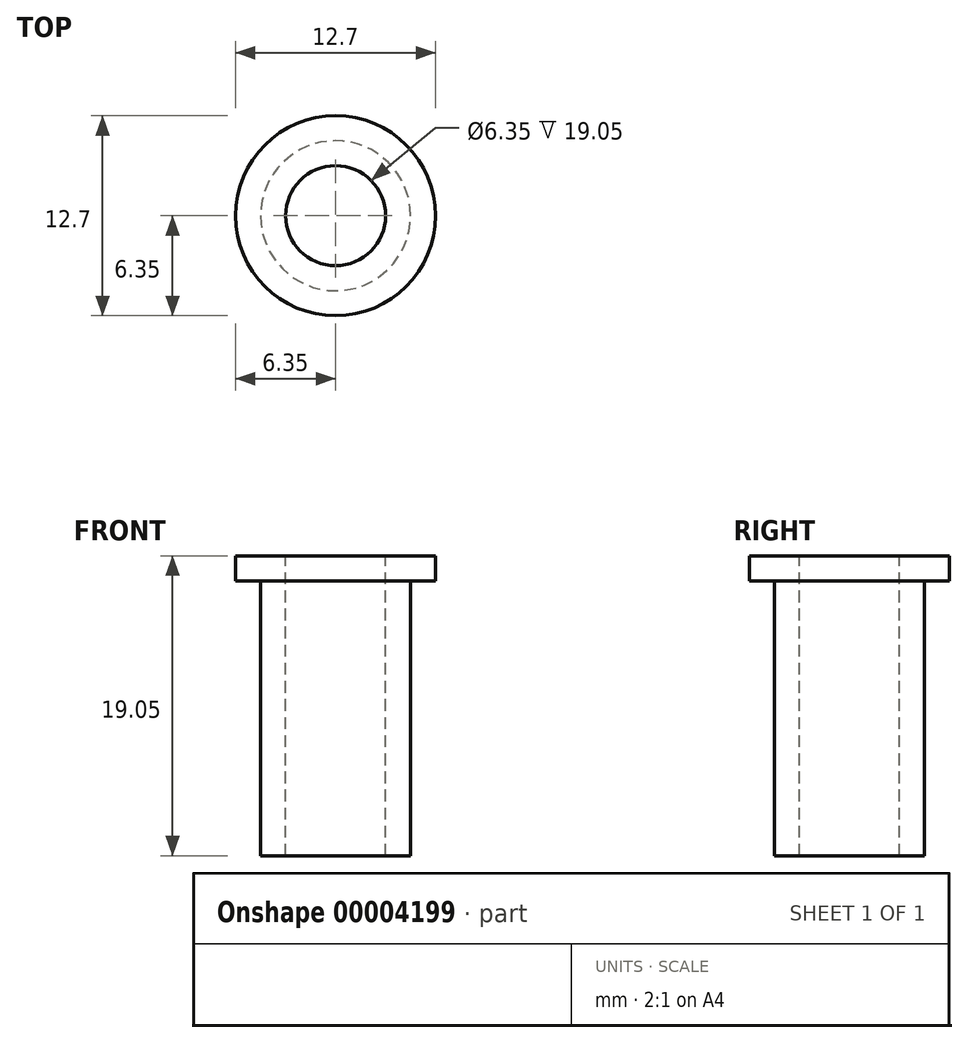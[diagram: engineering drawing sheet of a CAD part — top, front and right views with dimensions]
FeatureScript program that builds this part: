
annotation { "Feature Type Name" : "Feature", "Feature Type Description" : "" }
export const myFeature = defineFeature(function(context is Context, id is Id, definition is map)
    precondition{}
    {
        {
            var Q0;
            Q0=qCreatedBy(makeId("Front.planeOp"),FACE);
            var sketch = newSketch(context, id + "F0", { "sketchPlane" : qUnion([Q0])});
            skLineSegment(sketch, "E0", {"start": v(6.35, 0) * mm, "end": v(3.18, 0) * mm});
            skLineSegment(sketch, "E1", {"start": v(3.18, 0) * mm, "end": v(3.18, -19.05) * mm});
            skLineSegment(sketch, "E2", {"start": v(3.18, -19.05) * mm, "end": v(4.76, -19.05) * mm});
            skLineSegment(sketch, "E3", {"start": v(4.76, -19.05) * mm, "end": v(4.76, -1.59) * mm});
            skLineSegment(sketch, "E4", {"start": v(4.76, -1.59) * mm, "end": v(6.35, -1.59) * mm});
            skLineSegment(sketch, "E5", {"start": v(6.35, -1.59) * mm, "end": v(6.35, 0) * mm});
            skLineSegment(sketch, "E6", {"start": v(0, 0) * mm, "end": v(0, -18.07) * mm, "construction": true});
            skSolve(sketch);
        }
        {
            var Q0;
            Q0=makeQuery(id+"F0.imprint","IMPRINT",FACE,{"disambiguationData":[TD([[makeQuery(id+"F0.imprint","IMPRINT",EDGE,{"derivedFrom":sQuery(id+"F0.wireOp",EDGE,"E0")}),1.0]])]});
            var Q1;
            Q1=sQuery(id+"F0.wireOp",EDGE,"E6");
            revolve(context, id + "F1", {"entities" : qUnion([Q0]), "axis" : qUnion([Q1]), "revolveType" : RevolveType.FULL});
        }
    });
